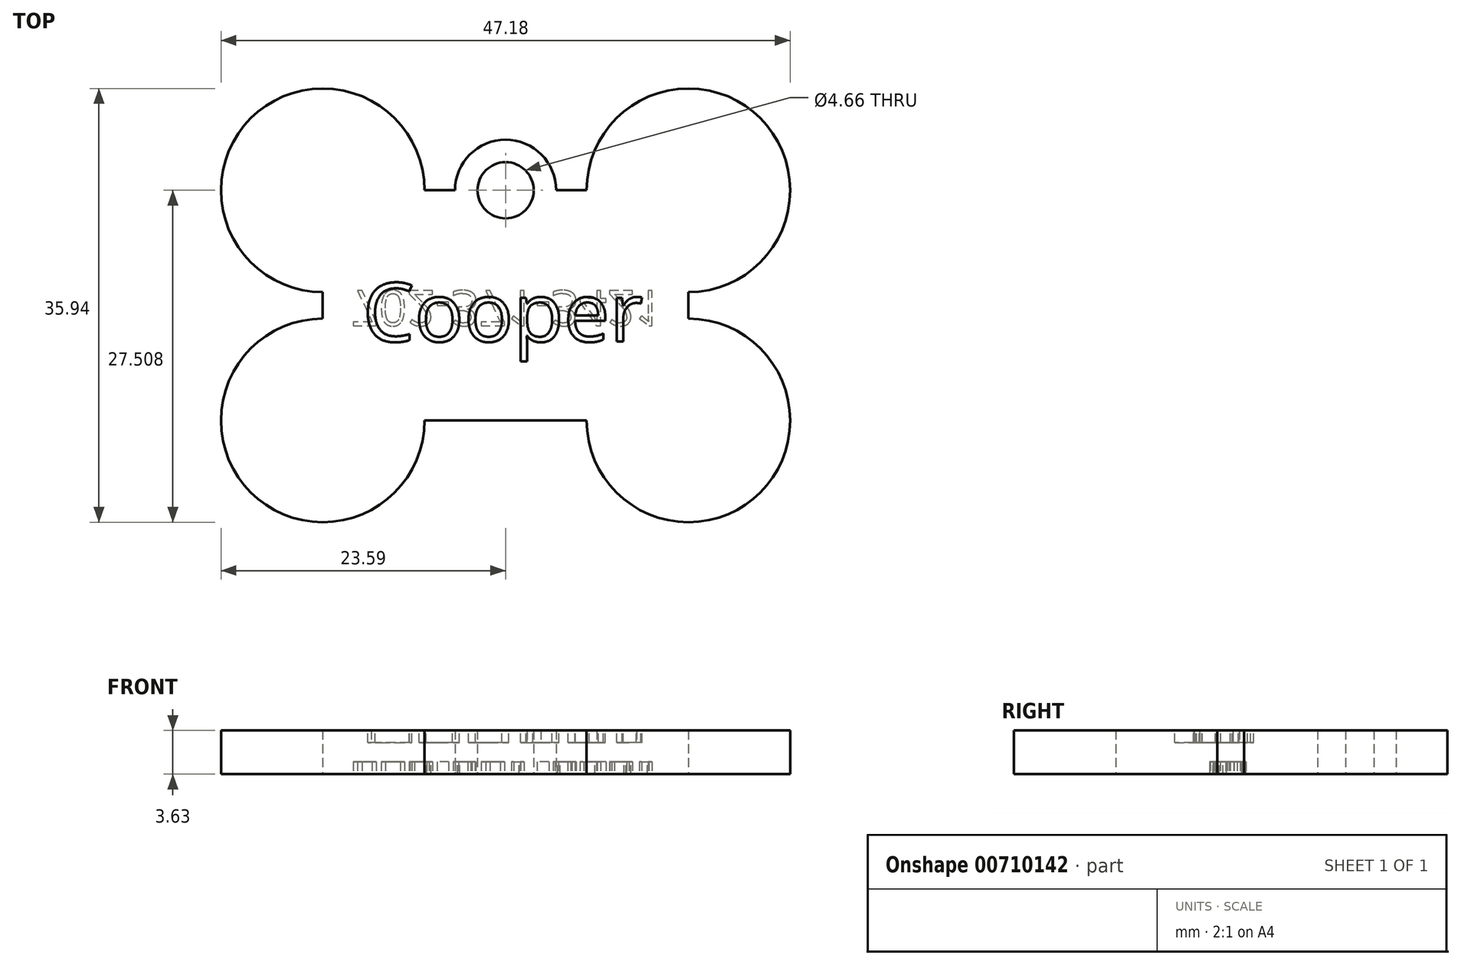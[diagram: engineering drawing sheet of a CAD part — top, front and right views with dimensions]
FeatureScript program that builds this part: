
annotation { "Feature Type Name" : "Feature", "Feature Type Description" : "" }
export const myFeature = defineFeature(function(context is Context, id is Id, definition is map)
    precondition{}
    {
        {
            var Q0;
            Q0=qCreatedBy(makeId("Top.planeOp"),FACE);
            var sketch = newSketch(context, id + "F0", { "sketchPlane" : qUnion([Q0])});
            skLineSegment(sketch, "E0.bottom", {"start": v(15.16, 9.54) * mm, "end": v(-15.16, 9.54) * mm});
            skLineSegment(sketch, "E0.top", {"start": v(15.16, -9.54) * mm, "end": v(-15.16, -9.54) * mm});
            skLineSegment(sketch, "E0.left", {"start": v(15.16, 9.54) * mm, "end": v(15.16, -9.54) * mm});
            skLineSegment(sketch, "E0.right", {"start": v(-15.16, 9.54) * mm, "end": v(-15.16, -9.54) * mm});
            skPoint(sketch, "E0.middle", {"position": v(0, 0) * mm});
            skSolve(sketch);
        }
        {
            var Q0;
            Q0=makeQuery(id+"F0.imprint","IMPRINT",FACE,{"disambiguationData":[TD([[makeQuery(id+"F0.imprint","IMPRINT",EDGE,{"derivedFrom":sQuery(id+"F0.wireOp",EDGE,"E0.bottom")}),1.0]])]});
            var sketch = newSketch(context, id + "F1", { "sketchPlane" : qUnion([Q0])});
            skArc(sketch, "E1", {"start": v(6.72, -9.54) * mm, "mid": v(21.12, -15.5) * mm, "end": v(15.16, -1.1) * mm});
            skArc(sketch, "E2", {"start": v(15.16, 1.1) * mm, "mid": v(21.12, 15.5) * mm, "end": v(6.72, 9.54) * mm});
            skArc(sketch, "E3", {"start": v(-15.16, -1.1) * mm, "mid": v(-21.12, -15.5) * mm, "end": v(-6.72, -9.54) * mm});
            skArc(sketch, "E4", {"start": v(-6.72, 9.54) * mm, "mid": v(-21.12, 15.5) * mm, "end": v(-15.16, 1.1) * mm});
            skLineSegment(sketch, "E5", {"start": v(-6.72, 9.54) * mm, "end": v(-4.19, 9.54) * mm});
            skLineSegment(sketch, "E6", {"start": v(6.72, -9.54) * mm, "end": v(-6.72, -9.54) * mm});
            skLineSegment(sketch, "E7", {"start": v(-15.16, -1.1) * mm, "end": v(-15.16, 1.1) * mm});
            skLineSegment(sketch, "E8", {"start": v(15.16, -1.1) * mm, "end": v(15.16, 1.1) * mm});
            skArc(sketch, "E9", {"start": v(4.19, 9.54) * mm, "mid": v(0, 13.73) * mm, "end": v(-4.19, 9.54) * mm});
            skCircle(sketch, "E10", {"center": v(0, 9.54) * mm, "radius": 2.33 * mm});
            skLineSegment(sketch, "E11.trimOffspring", {"start": v(4.19, 9.54) * mm, "end": v(6.72, 9.54) * mm});
            skSolve(sketch);
        }
        {
            var Q0;
            {var subQ0=sQuery(id+"F1.wireOp",EDGE,"E2");Q0=makeQuery(id+"F1.imprint","IMPRINT",FACE,{"disambiguationData":[TD([[makeQuery(id+"F1.imprint","IMPRINT",EDGE,{"derivedFrom":subQ0}),1.0]])]});}
            var Q1;
            {var subQ0=sQuery(id+"F1.wireOp",EDGE,"E1");Q1=makeQuery(id+"F1.imprint","IMPRINT",FACE,{"disambiguationData":[TD([[makeQuery(id+"F1.imprint","IMPRINT",EDGE,{"derivedFrom":subQ0}),1.0]])]});}
            var Q2;
            {var subQ0=sQuery(id+"F1.wireOp",EDGE,"E3");Q2=makeQuery(id+"F1.imprint","IMPRINT",FACE,{"disambiguationData":[TD([[makeQuery(id+"F1.imprint","IMPRINT",EDGE,{"derivedFrom":subQ0}),1.0]])]});}
            var Q3;
            {var subQ0=sQuery(id+"F1.wireOp",EDGE,"E4");Q3=makeQuery(id+"F1.imprint","IMPRINT",FACE,{"disambiguationData":[TD([[makeQuery(id+"F1.imprint","IMPRINT",EDGE,{"derivedFrom":subQ0}),1.0]])]});}
            var Q4;
            {var subQ13=sQuery(id+"F1.wireOp",EDGE,"E5");Q4=makeQuery(id+"F1.imprint","IMPRINT",FACE,{"disambiguationData":[TD([[makeQuery(id+"F1.imprint","IMPRINT",EDGE,{"derivedFrom":subQ13}),1.0]])]});}
            var Q5;
            {var subQ0=sQuery(id+"F1.wireOp",EDGE,"E9");Q5=makeQuery(id+"F1.imprint","IMPRINT",FACE,{"disambiguationData":[TD([[makeQuery(id+"F1.imprint","IMPRINT",EDGE,{"derivedFrom":subQ0}),1.0]])]});}
            extrude(context, id + "F2", {"entities" : qUnion([Q0, Q1, Q2, Q3, Q4, Q5]), "depth" : 3.6 * mm, "offsetDistance" : 25.4 * mm});
        }
        {
            var Q0;
            Q0=makeQuery(id+"F2.opExtrude","CAP_FACE",FACE,{"disambiguationData":[OSD([sQuery(id+"F1.wireOp",EDGE,"E1"),sQuery(id+"F1.wireOp",EDGE,"E2"),sQuery(id+"F1.wireOp",EDGE,"E3"),sQuery(id+"F1.wireOp",EDGE,"E4"),sQuery(id+"F1.wireOp",EDGE,"E5"),sQuery(id+"F1.wireOp",EDGE,"E6"),sQuery(id+"F1.wireOp",EDGE,"E7"),sQuery(id+"F1.wireOp",EDGE,"E8"),sQuery(id+"F1.wireOp",EDGE,"E9"),sQuery(id+"F1.wireOp",EDGE,"E10"),sQuery(id+"F1.wireOp",EDGE,"E11.trimOffspring")])],"isStart":false});
            var sketch = newSketch(context, id + "F3", { "sketchPlane" : qUnion([Q0])});
            skText(sketch, "E12", { "text": "cooper", "fontName": "OpenSans-Regular.ttf"});
            const initialGuessF3  = {"E12": [-0.015, -0.0034, 1, 0, 0.00649]};
            skSetInitialGuess(sketch, initialGuessF3);
            skSolve(sketch);
        }
        {
            var Q0;
            Q0 = qSketchRegion(id + "F3", true);
            var Q1;
            Q1=makeQuery(id+"F2.opExtrude","CAP_FACE",FACE,{"disambiguationData":[OSD([sQuery(id+"F1.wireOp",EDGE,"E1"),sQuery(id+"F1.wireOp",EDGE,"E2"),sQuery(id+"F1.wireOp",EDGE,"E3"),sQuery(id+"F1.wireOp",EDGE,"E4"),sQuery(id+"F1.wireOp",EDGE,"E5"),sQuery(id+"F1.wireOp",EDGE,"E6"),sQuery(id+"F1.wireOp",EDGE,"E7"),sQuery(id+"F1.wireOp",EDGE,"E8"),sQuery(id+"F1.wireOp",EDGE,"E9"),sQuery(id+"F1.wireOp",EDGE,"E10"),sQuery(id+"F1.wireOp",EDGE,"E11.trimOffspring")])],"isStart":true});
            extrude(context, id + "F4", {"entities" : qUnion([Q0, Q1]), "operationType" : NewBodyOperationType.ADD, "oppositeDirection" : true, "depth" : 0.04 * mm, "offsetDistance" : 25.4 * mm});
        }
        {
            var Q0;
            Q0=makeQuery(id+"F4.opExtrude","CAP_FACE",FACE,{"disambiguationData":[OSD([sQuery(id+"F1.wireOp",EDGE,"E1"),sQuery(id+"F1.wireOp",EDGE,"E2"),sQuery(id+"F1.wireOp",EDGE,"E3"),sQuery(id+"F1.wireOp",EDGE,"E4"),sQuery(id+"F1.wireOp",EDGE,"E5"),sQuery(id+"F1.wireOp",EDGE,"E6"),sQuery(id+"F1.wireOp",EDGE,"E7"),sQuery(id+"F1.wireOp",EDGE,"E8"),sQuery(id+"F1.wireOp",EDGE,"E9"),sQuery(id+"F1.wireOp",EDGE,"E10"),sQuery(id+"F1.wireOp",EDGE,"E11.trimOffspring")])],"isStart":false});
            var sketch = newSketch(context, id + "F5", { "sketchPlane" : qUnion([Q0])});
            skText(sketch, "E13", { "text": "702-371-3421", "fontName": "OpenSans-Regular.ttf"});
            const initialGuessF5  = {"E13": [-0.01283, -0.00122, 1, 0, 0.00293]};
            skSetInitialGuess(sketch, initialGuessF5);
            skSolve(sketch);
        }
        {
            var Q0;
            Q0 = qSketchRegion(id + "F5", true);
            var Q1;
            Q1=makeQuery(id+"F2.opExtrude","CAP_FACE",FACE,{"disambiguationData":[OSD([sQuery(id+"F1.wireOp",EDGE,"E1"),sQuery(id+"F1.wireOp",EDGE,"E2"),sQuery(id+"F1.wireOp",EDGE,"E3"),sQuery(id+"F1.wireOp",EDGE,"E4"),sQuery(id+"F1.wireOp",EDGE,"E5"),sQuery(id+"F1.wireOp",EDGE,"E6"),sQuery(id+"F1.wireOp",EDGE,"E7"),sQuery(id+"F1.wireOp",EDGE,"E8"),sQuery(id+"F1.wireOp",EDGE,"E9"),sQuery(id+"F1.wireOp",EDGE,"E10"),sQuery(id+"F1.wireOp",EDGE,"E11.trimOffspring")])],"isStart":false});
            extrude(context, id + "F6", {"entities" : qUnion([Q0, Q1]), "operationType" : NewBodyOperationType.REMOVE, "oppositeDirection" : true, "depth" : 1.02 * mm, "offsetDistance" : 25.4 * mm});
        }
        {
            var Q0;
            Q0=makeQuery(id+"F2.opExtrude","CAP_FACE",FACE,{"disambiguationData":[OSD([sQuery(id+"F1.wireOp",EDGE,"E1"),sQuery(id+"F1.wireOp",EDGE,"E2"),sQuery(id+"F1.wireOp",EDGE,"E3"),sQuery(id+"F1.wireOp",EDGE,"E4"),sQuery(id+"F1.wireOp",EDGE,"E5"),sQuery(id+"F1.wireOp",EDGE,"E6"),sQuery(id+"F1.wireOp",EDGE,"E7"),sQuery(id+"F1.wireOp",EDGE,"E8"),sQuery(id+"F1.wireOp",EDGE,"E9"),sQuery(id+"F1.wireOp",EDGE,"E10"),sQuery(id+"F1.wireOp",EDGE,"E11.trimOffspring")])],"isStart":false});
            var sketch = newSketch(context, id + "F7", { "sketchPlane" : qUnion([Q0])});
            skText(sketch, "E14", { "text": "Cooper", "fontName": "OpenSans-Regular.ttf"});
            const initialGuessF7  = {"E14": [-0.01184, -0.003, 1, 0, 0.00489]};
            skSetInitialGuess(sketch, initialGuessF7);
            skSolve(sketch);
        }
        {
            var Q0;
            Q0 = qSketchRegion(id + "F7", true);
            extrude(context, id + "F8", {"entities" : qUnion([Q0]), "operationType" : NewBodyOperationType.REMOVE, "oppositeDirection" : true, "depth" : 1.02 * mm, "offsetDistance" : 25.4 * mm});
        }
    });
